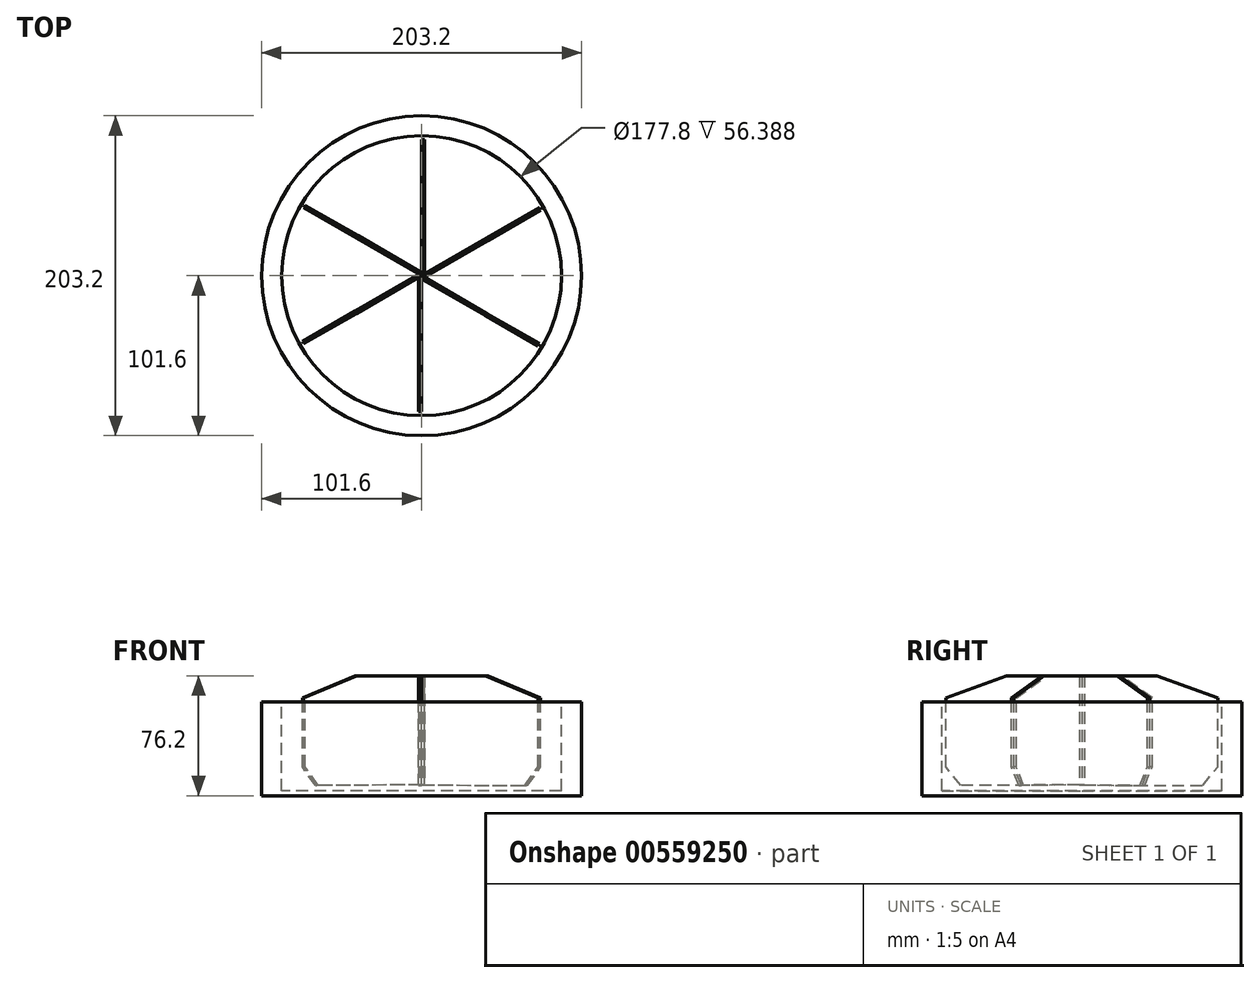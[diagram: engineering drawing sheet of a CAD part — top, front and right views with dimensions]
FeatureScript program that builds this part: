
annotation { "Feature Type Name" : "Feature", "Feature Type Description" : "" }
export const myFeature = defineFeature(function(context is Context, id is Id, definition is map)
    precondition{}
    {
        {
            var Q0;
            Q0=qCreatedBy(makeId("Top.planeOp"),FACE);
            var sketch = newSketch(context, id + "F0", { "sketchPlane" : qUnion([Q0])});
            skCircle(sketch, "E0", {"center": v(0, 0) * mm, "radius": 101.6 * mm});
            skSolve(sketch);
        }
        {
            var Q0;
            Q0 = qSketchRegion(id + "F0", true);
            extrude(context, id + "F1", {"entities" : qUnion([Q0]), "depth" : 59.44 * mm, "offsetDistance" : 25.4 * mm});
        }
        {
            var Q0;
            Q0=makeQuery(id+"F1.opExtrude","CAP_FACE",FACE,{"disambiguationData":[OSD([sQuery(id+"F0.wireOp",EDGE,"E0")])],"isStart":false});
            var sketch = newSketch(context, id + "F2", { "sketchPlane" : qUnion([Q0])});
            skCircle(sketch, "E1", {"center": v(0, 0) * mm, "radius": 88.9 * mm});
            skSolve(sketch);
        }
        {
            var Q0;
            Q0=makeQuery(id+"F2.imprint","IMPRINT",FACE,{"disambiguationData":[TD([[makeQuery(id+"F2.imprint","IMPRINT",EDGE,{"derivedFrom":sQuery(id+"F2.wireOp",EDGE,"E1")}),1.0]])]});
            extrude(context, id + "F3", {"entities" : qUnion([Q0]), "operationType" : NewBodyOperationType.REMOVE, "oppositeDirection" : true, "depth" : 56.4 * mm, "offsetDistance" : 25.4 * mm});
        }
        {
            var Q0;
            Q0=qCreatedBy(makeId("Right.planeOp"),FACE);
            var sketch = newSketch(context, id + "F4", { "sketchPlane" : qUnion([Q0])});
            skLineSegment(sketch, "E2", {"start": v(76.84, 6.43) * mm, "end": v(86.36, 18.45) * mm});
            skLineSegment(sketch, "E3", {"start": v(86.36, 18.45) * mm, "end": v(86.36, 62.11) * mm});
            skLineSegment(sketch, "E4", {"start": v(86.36, 62.11) * mm, "end": v(47.75, 76.2) * mm});
            skLineSegment(sketch, "E5", {"start": v(47.75, 76.2) * mm, "end": v(0, 76.2) * mm});
            skLineSegment(sketch, "E6", {"start": v(0, 76.2) * mm, "end": v(0, 6.94) * mm});
            skLineSegment(sketch, "E7", {"start": v(0, 6.94) * mm, "end": v(76.84, 6.43) * mm});
            skSolve(sketch);
        }
        {
            var Q0;
            Q0=makeQuery(id+"F4.imprint","IMPRINT",FACE,{"disambiguationData":[TD([[makeQuery(id+"F4.imprint","IMPRINT",EDGE,{"derivedFrom":sQuery(id+"F4.wireOp",EDGE,"E2")}),1.0]])]});
            extrude(context, id + "F5", {"entities" : qUnion([Q0]), "depth" : 1.78 * mm, "offsetDistance" : 25.4 * mm});
        }
        {
            var Q0;
            Q0=makeQuery(id+"F5.opExtrude","SWEPT_BODY",BODY,{"disambiguationData":[OSD([sQuery(id+"F4.wireOp",EDGE,"E2"),sQuery(id+"F4.wireOp",EDGE,"E3"),sQuery(id+"F4.wireOp",EDGE,"E4"),sQuery(id+"F4.wireOp",EDGE,"E5"),sQuery(id+"F4.wireOp",EDGE,"E6"),sQuery(id+"F4.wireOp",EDGE,"E7")])]});
            var Q1;
            Q1=makeQuery(id+"F1.opExtrude","CAP_EDGE",EDGE,{"disambiguationData":[OSD([sQuery(id+"F0.wireOp",EDGE,"E0")])],"isStart":false});
            circularPattern(context, id + "F6", {"entities" : qUnion([Q0]), "axis" : qUnion([Q1]), "angle" : 360 * degree, "instanceCount" : 6, "equalSpace" : true});
        }
        {
            var Q0;
            Q0=makeQuery(id+"F3.boolean.opBoolean","COPY",FACE,{"derivedFrom":makeQuery(id+"F3.opExtrude","CAP_FACE",FACE,{"disambiguationData":[OSD([sQuery(id+"F2.wireOp",EDGE,"E1")])],"isStart":false})});
            var sketch = newSketch(context, id + "F7", { "sketchPlane" : qUnion([Q0])});
            skCircle(sketch, "E8", {"center": v(0, 0) * mm, "radius": 1.27 * mm});
            skSolve(sketch);
        }
        {
            var Q0;
            Q0=sQuery(id+"F7.wireOp",EDGE,"E8");
            extrude(context, id + "F8", {"bodyType" : ToolBodyType.SURFACE, "surfaceEntities" : qUnion([Q0]), "depth" : 120.4 * mm, "offsetDistance" : 25.4 * mm});
        }
    });
